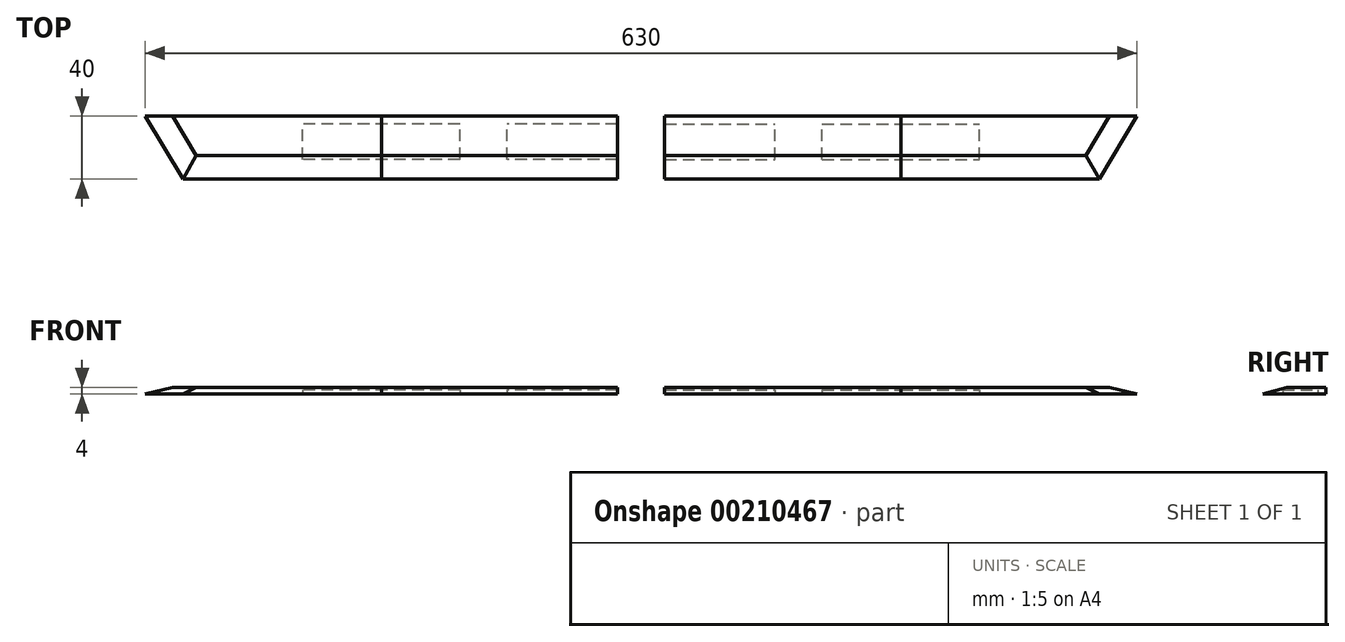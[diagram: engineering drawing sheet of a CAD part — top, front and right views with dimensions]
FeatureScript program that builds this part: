
annotation { "Feature Type Name" : "Feature", "Feature Type Description" : "" }
export const myFeature = defineFeature(function(context is Context, id is Id, definition is map)
    precondition{}
    {
        {
            var Q0;
            Q0=qCreatedBy(makeId("Top.planeOp"),FACE);
            var sketch = newSketch(context, id + "F0", { "sketchPlane" : qUnion([Q0])});
            skLineSegment(sketch, "E0", {"start": v(0, 0) * mm, "end": v(-15, 0) * mm});
            skLineSegment(sketch, "E1", {"start": v(-15, 0) * mm, "end": v(-15, 40) * mm});
            skLineSegment(sketch, "E2", {"start": v(-15, 40) * mm, "end": v(-315, 40) * mm});
            skLineSegment(sketch, "E3", {"start": v(-15, 0) * mm, "end": v(-291, 0) * mm});
            skLineSegment(sketch, "E4", {"start": v(-291, 0) * mm, "end": v(-315, 40) * mm});
            skLineSegment(sketch, "E5", {"start": v(0, 0) * mm, "end": v(0, 40) * mm});
            skLineSegment(sketch, "E6", {"start": v(0, 40) * mm, "end": v(-15, 40) * mm});
            skLineSegment(sketch, "E7.MirrorCS", {"start": v(15, 0) * mm, "end": v(15, 40) * mm});
            skLineSegment(sketch, "E8.MirrorCS", {"start": v(15, 40) * mm, "end": v(315, 40) * mm});
            skLineSegment(sketch, "E9.MirrorCS", {"start": v(15, 0) * mm, "end": v(291, 0) * mm});
            skLineSegment(sketch, "E10.MirrorCS", {"start": v(291, 0) * mm, "end": v(315, 40) * mm});
            skLineSegment(sketch, "E11", {"start": v(-15, 40) * mm, "end": v(-165, 40) * mm});
            skLineSegment(sketch, "E12", {"start": v(-165, 40) * mm, "end": v(-165, 0) * mm});
            skLineSegment(sketch, "E13", {"start": v(165, 40) * mm, "end": v(165, 0) * mm});
            skSolve(sketch);
        }
        {
            var Q0;
            Q0=makeQuery(id+"F0.imprint","IMPRINT",FACE,{"disambiguationData":[TD([[makeQuery(id+"F0.imprint","IMPRINT",EDGE,{"derivedFrom":sQuery(id+"F0.wireOp",EDGE,"E2")}),1.0]])]});
            var Q1;
            {var subQ0=sQuery(id+"F0.wireOp",EDGE,"E10.MirrorCS");Q1=makeQuery(id+"F0.imprint","IMPRINT",FACE,{"disambiguationData":[TD([[makeQuery(id+"F0.imprint","IMPRINT",EDGE,{"derivedFrom":subQ0}),1.0]])]});}
            extrude(context, id + "F1", {"entities" : qUnion([Q0, Q1]), "depth" : 4 * mm});
        }
        {
            var Q0;
            {var subQ0=sQuery(id+"F0.wireOp",EDGE,"E1");Q0=makeQuery(id+"F0.imprint","IMPRINT",FACE,{"disambiguationData":[TD([[makeQuery(id+"F0.imprint","IMPRINT",EDGE,{"derivedFrom":subQ0}),1.0]])]});}
            var Q1;
            {var subQ0=sQuery(id+"F0.wireOp",EDGE,"E7.MirrorCS");Q1=makeQuery(id+"F0.imprint","IMPRINT",FACE,{"disambiguationData":[TD([[makeQuery(id+"F0.imprint","IMPRINT",EDGE,{"derivedFrom":subQ0}),-1.0]])]});}
            extrude(context, id + "F2", {"entities" : qUnion([Q0, Q1]), "depth" : 4 * mm});
        }
        {
            var Q0;
            Q0=makeQuery(id+"F1.opExtrude","CAP_EDGE",EDGE,{"disambiguationData":[OSD([sQuery(id+"F0.wireOp",EDGE,"E9.MirrorCS")])],"isStart":false});
            var Q1;
            Q1=makeQuery(id+"F1.opExtrude","CAP_EDGE",EDGE,{"disambiguationData":[OSD([sQuery(id+"F0.wireOp",EDGE,"E10.MirrorCS")])],"isStart":false});
            var Q2;
            Q2=makeQuery(id+"F2.opExtrude","CAP_EDGE",EDGE,{"disambiguationData":[OSD([sQuery(id+"F0.wireOp",EDGE,"E9.MirrorCS")])],"isStart":false});
            chamfer(context, id + "F3", {"entities" : qUnion([Q0, Q1, Q2]), "chamferType" : ChamferType.TWO_OFFSETS, "width1" : 15 * mm, "oppositeDirection" : false, "width2" : 4 * mm, "tangentPropagation" : true});
        }
        {
            var Q0;
            Q0=makeQuery(id+"F1.opExtrude","CAP_EDGE",EDGE,{"disambiguationData":[OSD([sQuery(id+"F0.wireOp",EDGE,"E0"),sQuery(id+"F0.wireOp",EDGE,"E3")])],"isStart":false});
            var Q1;
            Q1=makeQuery(id+"F1.opExtrude","CAP_EDGE",EDGE,{"disambiguationData":[OSD([sQuery(id+"F0.wireOp",EDGE,"E4")])],"isStart":false});
            var Q2;
            Q2=makeQuery(id+"F2.opExtrude","CAP_EDGE",EDGE,{"disambiguationData":[OSD([sQuery(id+"F0.wireOp",EDGE,"E3")])],"isStart":false});
            chamfer(context, id + "F4", {"entities" : qUnion([Q0, Q1, Q2]), "chamferType" : ChamferType.TWO_OFFSETS, "width1" : 4 * mm, "oppositeDirection" : false, "width2" : 15 * mm, "tangentPropagation" : true});
        }
        {
            var Q0;
            {var subQ0=sQuery(id+"F0.wireOp",EDGE,"E7.MirrorCS");Q0=makeQuery(id+"F0.imprint","IMPRINT",FACE,{"disambiguationData":[TD([[makeQuery(id+"F0.imprint","IMPRINT",EDGE,{"derivedFrom":subQ0}),-1.0]])]});}
            var sketch = newSketch(context, id + "F5", { "sketchPlane" : qUnion([Q0])});
            skLineSegment(sketch, "E14", {"start": v(0, 0) * mm, "end": v(15, 0) * mm});
            skLineSegment(sketch, "E15", {"start": v(15, 0) * mm, "end": v(15, 12.5) * mm});
            skLineSegment(sketch, "E16.bottom", {"start": v(15, 12.5) * mm, "end": v(85, 12.5) * mm});
            skLineSegment(sketch, "E16.top", {"start": v(15, 35) * mm, "end": v(85, 35) * mm});
            skLineSegment(sketch, "E16.left", {"start": v(15, 12.5) * mm, "end": v(15, 35) * mm});
            skLineSegment(sketch, "E16.right", {"start": v(85, 12.5) * mm, "end": v(85, 35) * mm});
            skLineSegment(sketch, "E17", {"start": v(85, 12.5) * mm, "end": v(115, 12.5) * mm});
            skLineSegment(sketch, "E18.bottom", {"start": v(115, 12.5) * mm, "end": v(215, 12.5) * mm});
            skLineSegment(sketch, "E18.top", {"start": v(115, 35) * mm, "end": v(215, 35) * mm});
            skLineSegment(sketch, "E18.left", {"start": v(115, 12.5) * mm, "end": v(115, 35) * mm});
            skLineSegment(sketch, "E18.right", {"start": v(215, 12.5) * mm, "end": v(215, 35) * mm});
            skLineSegment(sketch, "E19", {"start": v(0, 0) * mm, "end": v(0, 55.55) * mm});
            skLineSegment(sketch, "E20.MirrorCS", {"start": v(-15, 12.5) * mm, "end": v(-15, 35) * mm});
            skLineSegment(sketch, "E21.MirrorCS", {"start": v(-15, 12.5) * mm, "end": v(-85, 12.5) * mm});
            skLineSegment(sketch, "E22.MirrorCS", {"start": v(-15, 35) * mm, "end": v(-85, 35) * mm});
            skLineSegment(sketch, "E23.MirrorCS", {"start": v(-85, 12.5) * mm, "end": v(-85, 35) * mm});
            skLineSegment(sketch, "E24.MirrorCS", {"start": v(-115, 12.5) * mm, "end": v(-115, 35) * mm});
            skLineSegment(sketch, "E25.MirrorCS", {"start": v(-115, 35) * mm, "end": v(-215, 35) * mm});
            skLineSegment(sketch, "E26.MirrorCS", {"start": v(-115, 12.5) * mm, "end": v(-215, 12.5) * mm});
            skLineSegment(sketch, "E27.MirrorCS", {"start": v(-215, 12.5) * mm, "end": v(-215, 35) * mm});
            skLineSegment(sketch, "E28.MirrorCS", {"start": v(-85, 12.5) * mm, "end": v(-115, 12.5) * mm});
            skLineSegment(sketch, "E29.MirrorCS", {"start": v(-15, 0) * mm, "end": v(-15, 12.5) * mm});
            skLineSegment(sketch, "E30.MirrorCS", {"start": v(0, 0) * mm, "end": v(-15, 0) * mm});
            skSolve(sketch);
        }
        {
            var Q0;
            Q0 = qSketchRegion(id + "F5", true);
            extrude(context, id + "F6", {"entities" : qUnion([Q0]), "operationType" : NewBodyOperationType.REMOVE, "depth" : 2.5 * mm});
        }
    });
